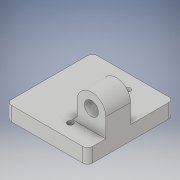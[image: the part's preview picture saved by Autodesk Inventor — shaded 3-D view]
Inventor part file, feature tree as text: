
AUTODESK INVENTOR PART (.ipt)
format: ipt  version: 2018 (Build 220112000, 112)  size: 286,720 bytes
history: native  units: in
note: dims shown in document units (in); Inventor stores cm internally (conversion verified against a paired STEP export)
features: extrude x3, sketch x3, fillet x2, chamfer x1
ambient origin geometry x8: Origin, YZ Plane, XZ Plane, XY Plane, X Axis, Y Axis, Z Axis, Center Point
bodies: Solid1 (feature_tree)
feature tree (9):
  extrude  "Extrusion1"  Depth=0.85in
  extrude  "Extrusion2"  Depth=0.05in
  fillet  "Fillet1"  Radius=0.05in
  extrude  "Extrusion4"  Depth=0.05in
  chamfer  "Chamfer1"  Distance=0.09in
  fillet  "Fillet2"  Radius=0.09in
  sketch  "Sketch1"  dims[d0=0.9in d1=0.85in]
  sketch  "Sketch2"  dims[d2=0.06in d3=0.06in d4=0.05in]
  sketch  "Sketch3"  dims[d6=0.05in d10=0.6in d11=0.09in d12=0.09in d13=0.4in d14=0.65in d15=0.15in d16=0.0in d17=0.26in d18=0.3in d19=0.35in d20=0.0in d21=0.15in d22=0.146in d26=0.05in d27=0.125in d28=45.0deg d29=0.05in d30=0.602in d31=0.119in d32=1.0in d33=0.0in]
